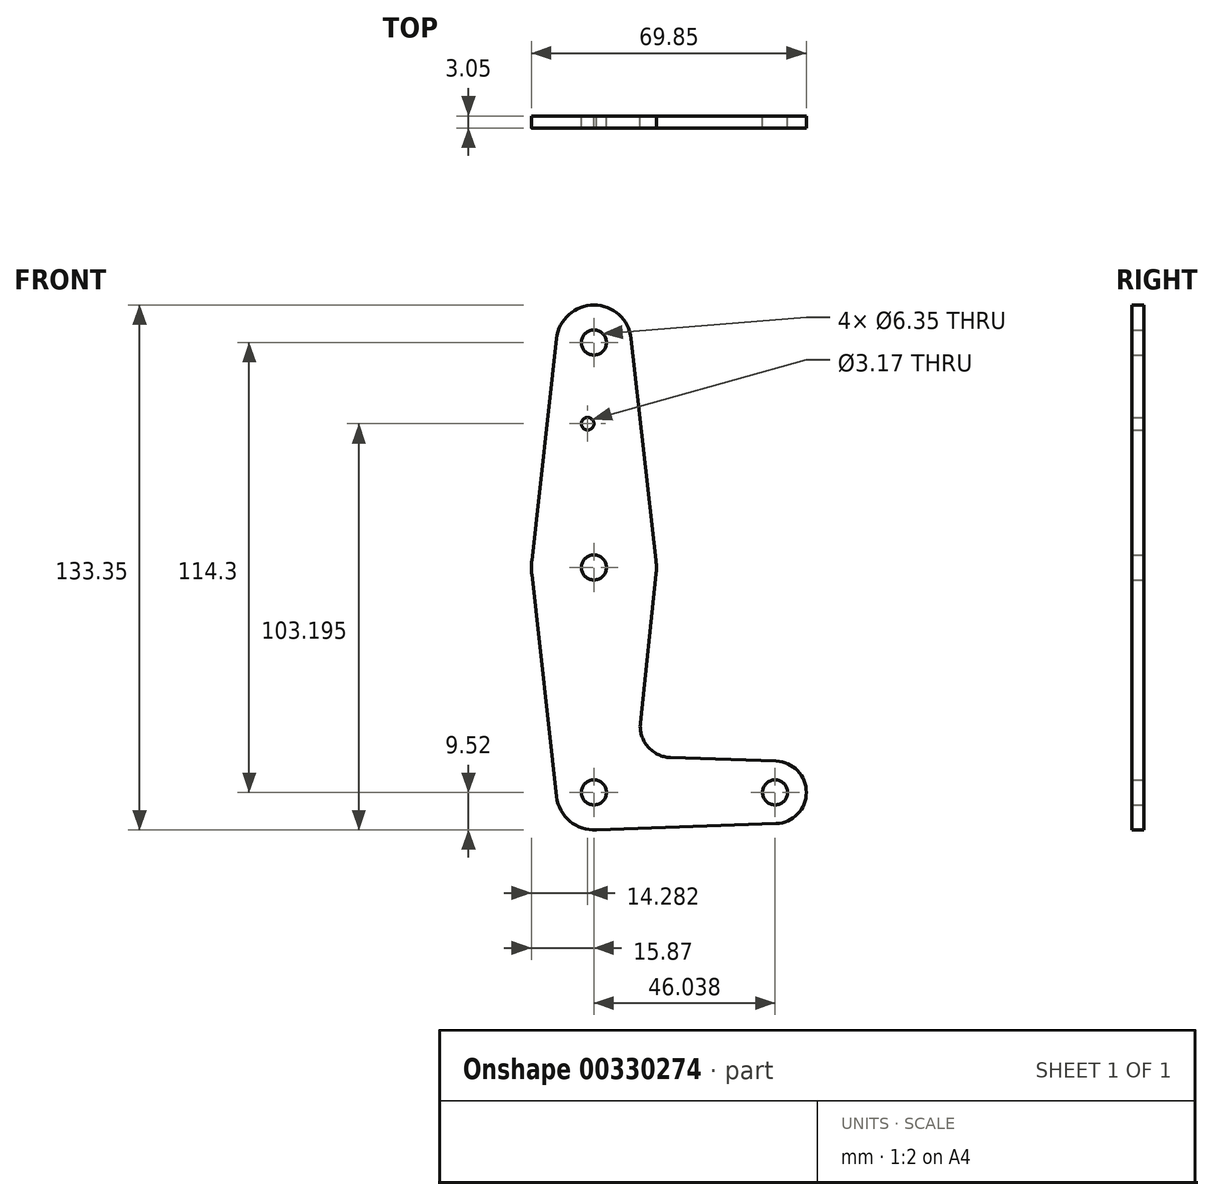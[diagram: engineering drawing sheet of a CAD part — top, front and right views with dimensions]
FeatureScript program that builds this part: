
annotation { "Feature Type Name" : "Feature", "Feature Type Description" : "" }
export const myFeature = defineFeature(function(context is Context, id is Id, definition is map)
    precondition{}
    {
        {
            var Q0;
            Q0=qCreatedBy(makeId("Front.planeOp"),FACE);
            var sketch = newSketch(context, id + "F0", { "sketchPlane" : qUnion([Q0])});
            skLineSegment(sketch, "E0", {"start": v(0, 114.3) * mm, "end": v(0, 0) * mm, "construction": true});
            skLineSegment(sketch, "E1", {"start": v(0, 0) * mm, "end": v(46.04, 0) * mm, "construction": true});
            skCircle(sketch, "E2", {"center": v(0, 114.3) * mm, "radius": 9.53 * mm});
            skCircle(sketch, "E3", {"center": v(0, 0) * mm, "radius": 9.53 * mm});
            skCircle(sketch, "E4", {"center": v(46.04, 0) * mm, "radius": 7.94 * mm});
            skCircle(sketch, "E5", {"center": v(0, 57.15) * mm, "radius": 15.88 * mm});
            skLineSegment(sketch, "E6", {"start": v(-9.47, 115.36) * mm, "end": v(-15.78, 58.91) * mm});
            skLineSegment(sketch, "E7", {"start": v(0, -9.53) * mm, "end": v(46.31, -7.93) * mm});
            skLineSegment(sketch, "E8", {"start": v(46.31, 7.93) * mm, "end": v(19.45, 8.86) * mm});
            skLineSegment(sketch, "E9", {"start": v(11.81, 17.64) * mm, "end": v(15.79, 55.5) * mm});
            skLineSegment(sketch, "E10", {"start": v(15.78, 58.91) * mm, "end": v(9.47, 115.36) * mm});
            skLineSegment(sketch, "E11", {"start": v(-15.78, 55.39) * mm, "end": v(-9.47, -1.06) * mm});
            skCircle(sketch, "E12", {"center": v(-1.59, 93.68) * mm, "radius": 1.59 * mm});
            skCircle(sketch, "E13", {"center": v(0, 0) * mm, "radius": 3.18 * mm});
            skCircle(sketch, "E14", {"center": v(46.04, 0) * mm, "radius": 3.18 * mm});
            skCircle(sketch, "E15", {"center": v(0, 57.15) * mm, "radius": 3.18 * mm});
            skCircle(sketch, "E16", {"center": v(0, 114.3) * mm, "radius": 3.18 * mm});
            skArc(sketch, "E17.filletArc", {"start": v(11.81, 17.64) * mm, "mid": v(13.72, 11.59) * mm, "end": v(19.45, 8.86) * mm});
            skSolve(sketch);
        }
        {
            var Q0;
            Q0 = qSketchRegion(id + "F0", true);
            extrude(context, id + "F1", {"entities" : qUnion([Q0]), "depth" : 3.05 * mm});
        }
    });
